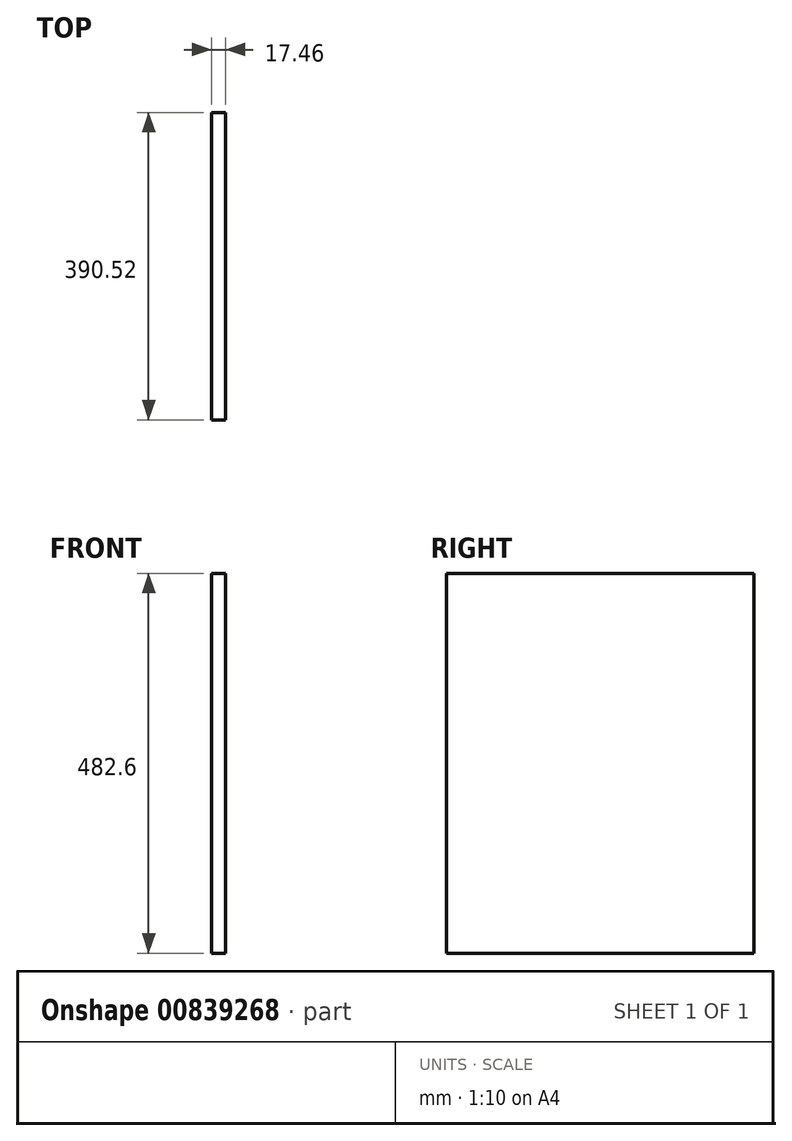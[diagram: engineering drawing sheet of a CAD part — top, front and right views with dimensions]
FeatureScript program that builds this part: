
annotation { "Feature Type Name" : "Feature", "Feature Type Description" : "" }
export const myFeature = defineFeature(function(context is Context, id is Id, definition is map)
    precondition{}
    {
        {
            var Q0;
            Q0=qCreatedBy(makeId("Right.planeOp"),FACE);
            var sketch = newSketch(context, id + "F0", { "sketchPlane" : qUnion([Q0])});
            skLineSegment(sketch, "E0.bottom", {"start": v(-202.14, 368.05) * mm, "end": v(188.38, 368.05) * mm});
            skLineSegment(sketch, "E0.top", {"start": v(-202.14, -114.55) * mm, "end": v(188.38, -114.55) * mm});
            skLineSegment(sketch, "E0.left", {"start": v(-202.14, 368.05) * mm, "end": v(-202.14, -114.55) * mm});
            skLineSegment(sketch, "E0.right", {"start": v(188.38, 368.05) * mm, "end": v(188.38, -114.55) * mm});
            skSolve(sketch);
        }
        {
            var Q0;
            Q0 = qSketchRegion(id + "F0", true);
            extrude(context, id + "F1", {"entities" : qUnion([Q0]), "depth" : 17.46 * mm, "offsetDistance" : 25.4 * mm});
        }
    });
